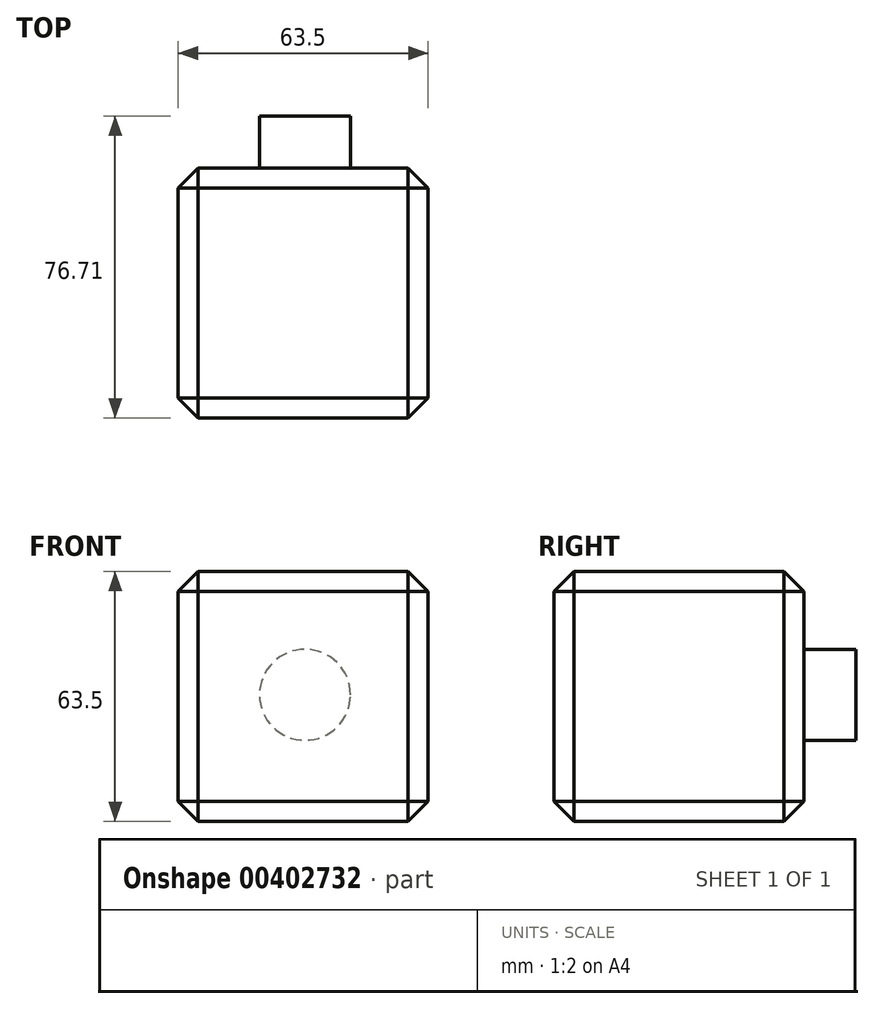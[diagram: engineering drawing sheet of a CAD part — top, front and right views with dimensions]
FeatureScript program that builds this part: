
annotation { "Feature Type Name" : "Feature", "Feature Type Description" : "" }
export const myFeature = defineFeature(function(context is Context, id is Id, definition is map)
    precondition{}
    {
        {
            var Q0;
            Q0=qCreatedBy(makeId("Front.planeOp"),FACE);
            var sketch = newSketch(context, id + "F0", { "sketchPlane" : qUnion([Q0])});
            skLineSegment(sketch, "E0", {"start": v(-36.42, -34.71) * mm, "end": v(-36.42, 28.79) * mm});
            skLineSegment(sketch, "E1", {"start": v(-36.42, 28.79) * mm, "end": v(27.08, 28.79) * mm});
            skLineSegment(sketch, "E2", {"start": v(27.08, 28.79) * mm, "end": v(27.08, -34.71) * mm});
            skLineSegment(sketch, "E3", {"start": v(27.08, -34.71) * mm, "end": v(-36.42, -34.71) * mm});
            skSolve(sketch);
        }
        {
            var Q0;
            Q0=makeQuery(id+"F0.imprint","IMPRINT",FACE,{"disambiguationData":[TD([[makeQuery(id+"F0.imprint","IMPRINT",EDGE,{"derivedFrom":sQuery(id+"F0.wireOp",EDGE,"E0")}),-1.0]])]});
            extrude(context, id + "F1", {"entities" : qUnion([Q0]), "oppositeDirection" : true, "depth" : 63.5 * mm});
        }
        {
            var Q0;
            Q0=makeQuery(id+"F1.opExtrude","CAP_EDGE",EDGE,{"disambiguationData":[OSD([sQuery(id+"F0.wireOp",EDGE,"E1")])],"isStart":true});
            var Q1;
            Q1=makeQuery(id+"F1.opExtrude","SWEPT_EDGE",EDGE,{"disambiguationData":[OSD([sQuery(id+"F0.wireOp",EDGE,"E1"),sQuery(id+"F0.wireOp",EDGE,"E2")])]});
            var Q2;
            Q2=makeQuery(id+"F1.opExtrude","SWEPT_EDGE",EDGE,{"disambiguationData":[OSD([sQuery(id+"F0.wireOp",EDGE,"E0"),sQuery(id+"F0.wireOp",EDGE,"E1")])]});
            var Q3;
            Q3=makeQuery(id+"F1.opExtrude","CAP_EDGE",EDGE,{"disambiguationData":[OSD([sQuery(id+"F0.wireOp",EDGE,"E1")])],"isStart":false});
            var Q4;
            Q4=makeQuery(id+"F1.opExtrude","CAP_EDGE",EDGE,{"disambiguationData":[OSD([sQuery(id+"F0.wireOp",EDGE,"E2")])],"isStart":true});
            var Q5;
            Q5=makeQuery(id+"F1.opExtrude","CAP_EDGE",EDGE,{"disambiguationData":[OSD([sQuery(id+"F0.wireOp",EDGE,"E2")])],"isStart":false});
            var Q6;
            Q6=makeQuery(id+"F1.opExtrude","CAP_EDGE",EDGE,{"disambiguationData":[OSD([sQuery(id+"F0.wireOp",EDGE,"E0")])],"isStart":true});
            var Q7;
            Q7=makeQuery(id+"F1.opExtrude","CAP_EDGE",EDGE,{"disambiguationData":[OSD([sQuery(id+"F0.wireOp",EDGE,"E0")])],"isStart":false});
            var Q8;
            Q8=makeQuery(id+"F1.opExtrude","CAP_EDGE",EDGE,{"disambiguationData":[OSD([sQuery(id+"F0.wireOp",EDGE,"E3")])],"isStart":false});
            var Q9;
            Q9=makeQuery(id+"F1.opExtrude","SWEPT_EDGE",EDGE,{"disambiguationData":[OSD([sQuery(id+"F0.wireOp",EDGE,"E2"),sQuery(id+"F0.wireOp",EDGE,"E3")])]});
            var Q10;
            Q10=makeQuery(id+"F1.opExtrude","CAP_EDGE",EDGE,{"disambiguationData":[OSD([sQuery(id+"F0.wireOp",EDGE,"E3")])],"isStart":true});
            var Q11;
            Q11=makeQuery(id+"F1.opExtrude","SWEPT_EDGE",EDGE,{"disambiguationData":[OSD([sQuery(id+"F0.wireOp",EDGE,"E0"),sQuery(id+"F0.wireOp",EDGE,"E3")])]});
            chamfer(context, id + "F2", {"entities" : qUnion([Q0, Q1, Q2, Q3, Q4, Q5, Q6, Q7, Q8, Q9, Q10, Q11]), "width" : 5.08 * mm, "tangentPropagation" : true});
        }
        {
            var Q0;
            Q0=makeQuery(id+"F1.opExtrude","CAP_FACE",FACE,{"disambiguationData":[OSD([sQuery(id+"F0.wireOp",EDGE,"E0"),sQuery(id+"F0.wireOp",EDGE,"E1"),sQuery(id+"F0.wireOp",EDGE,"E2"),sQuery(id+"F0.wireOp",EDGE,"E3")])],"isStart":true});
            var sketch = newSketch(context, id + "F3", { "sketchPlane" : qUnion([Q0])});
            skCircle(sketch, "E4", {"center": v(-4.2, -2.54) * mm, "radius": 11.56 * mm});
            skSolve(sketch);
        }
        {
            var Q0;
            Q0=makeQuery(id+"F3.imprint","IMPRINT",FACE,{"disambiguationData":[TD([[makeQuery(id+"F3.imprint","IMPRINT",EDGE,{"derivedFrom":sQuery(id+"F3.wireOp",EDGE,"E4")}),1.0]])]});
            extrude(context, id + "F4", {"entities" : qUnion([Q0]), "operationType" : NewBodyOperationType.ADD, "oppositeDirection" : true, "depth" : 76.7 * mm});
        }
    });
